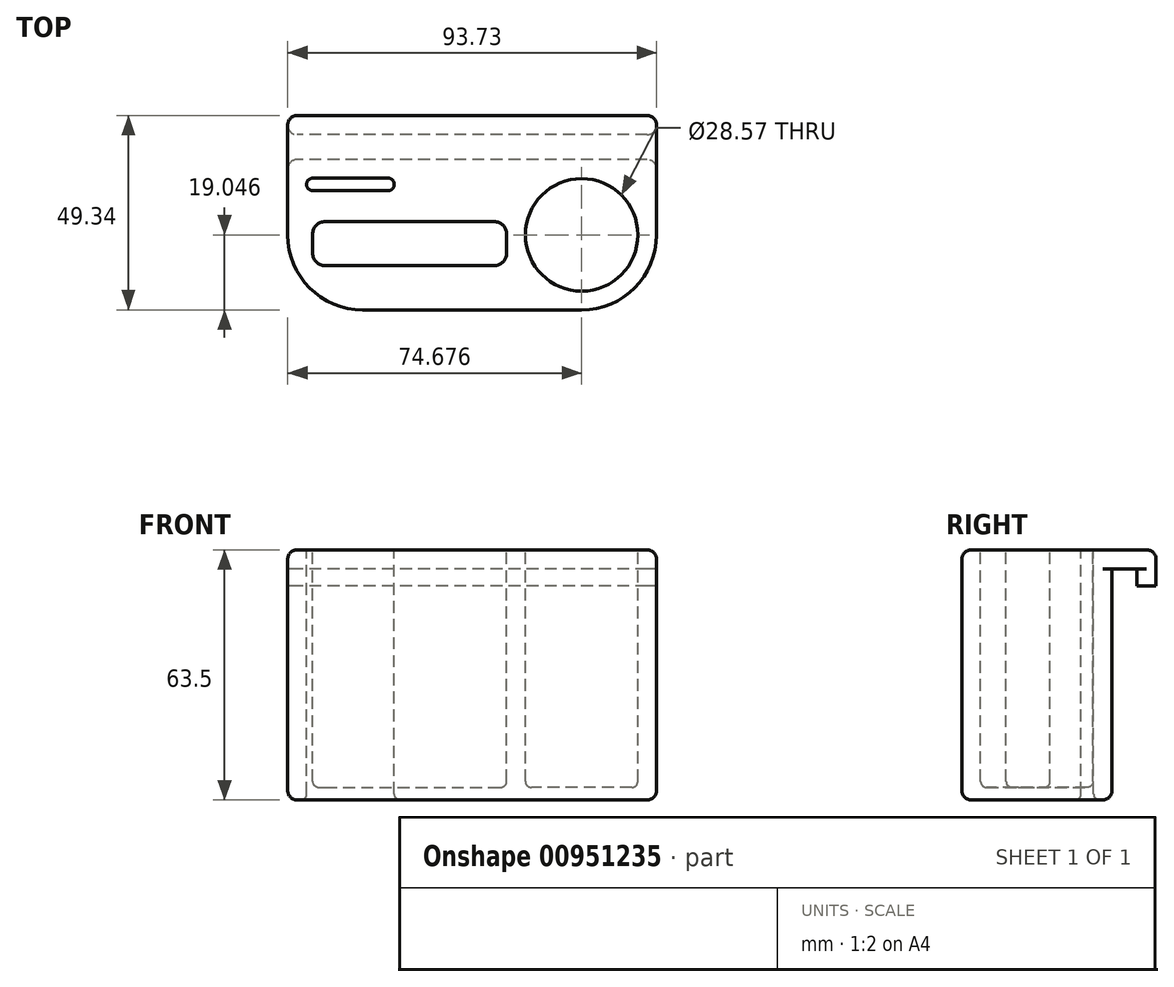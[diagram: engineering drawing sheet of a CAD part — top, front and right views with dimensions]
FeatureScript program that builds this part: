
annotation { "Feature Type Name" : "Feature", "Feature Type Description" : "" }
export const myFeature = defineFeature(function(context is Context, id is Id, definition is map)
    precondition{}
    {
        {
            var Q0;
            Q0=qCreatedBy(makeId("Right.planeOp"),FACE);
            var sketch = newSketch(context, id + "F0", { "sketchPlane" : qUnion([Q0])});
            skLineSegment(sketch, "E0", {"start": v(0, 0) * mm, "end": v(-6.35, 0) * mm});
            skLineSegment(sketch, "E1", {"start": v(-6.35, 0) * mm, "end": v(-6.35, -58.67) * mm});
            skLineSegment(sketch, "E2", {"start": v(-6.35, -58.67) * mm, "end": v(-11.18, -58.67) * mm});
            skLineSegment(sketch, "E3", {"start": v(-11.18, -58.67) * mm, "end": v(-11.18, 4.83) * mm});
            skLineSegment(sketch, "E4", {"start": v(-11.18, 4.83) * mm, "end": v(4.83, 4.83) * mm});
            skLineSegment(sketch, "E5", {"start": v(4.83, 4.83) * mm, "end": v(4.83, -4.32) * mm});
            skLineSegment(sketch, "E6", {"start": v(4.83, -4.32) * mm, "end": v(0, -4.32) * mm});
            skLineSegment(sketch, "E7", {"start": v(0, -4.32) * mm, "end": v(0, 0) * mm});
            skSolve(sketch);
        }
        {
            var Q0;
            Q0 = qSketchRegion(id + "F0", true);
            extrude(context, id + "F1", {"entities" : qUnion([Q0]), "depth" : 93.73 * mm, "offsetDistance" : 25.4 * mm});
        }
        {
            var Q0;
            Q0=makeQuery(id+"F1.opExtrude","SWEPT_FACE",FACE,{"disambiguationData":[OSD([sQuery(id+"F0.wireOp",EDGE,"E4")])]});
            var sketch = newSketch(context, id + "F2", { "sketchPlane" : qUnion([Q0])});
            skCircle(sketch, "E8", {"center": v(74.68, -25.46) * mm, "radius": 14.29 * mm});
            skLineSegment(sketch, "E9", {"start": v(93.73, -11.18) * mm, "end": v(93.73, -25.46) * mm});
            skLineSegment(sketch, "E10", {"start": v(74.68, -44.51) * mm, "end": v(19.05, -44.51) * mm});
            skLineSegment(sketch, "E11", {"start": v(0, -25.46) * mm, "end": v(0, -11.18) * mm});
            skLineSegment(sketch, "E12", {"start": v(0, -11.18) * mm, "end": v(93.73, -11.18) * mm});
            skPoint(sketch, "E13.visualSharp", {"position": v(93.73, -44.51) * mm});
            skArc(sketch, "E13.filletArc", {"start": v(74.68, -44.51) * mm, "mid": v(88.15, -38.93) * mm, "end": v(93.73, -25.46) * mm});
            skPoint(sketch, "E14.visualSharp", {"position": v(0, -44.51) * mm});
            skArc(sketch, "E14.filletArc", {"start": v(0, -25.46) * mm, "mid": v(5.58, -38.93) * mm, "end": v(19.05, -44.51) * mm});
            skSolve(sketch);
        }
        {
            var Q0;
            Q0 = qSketchRegion(id + "F2", true);
            var Q1;
            Q1=makeQuery(id+"F1.opExtrude","SWEPT_FACE",FACE,{"disambiguationData":[OSD([sQuery(id+"F0.wireOp",EDGE,"E2")])]});
            extrude(context, id + "F3", {"entities" : qUnion([Q0]), "operationType" : NewBodyOperationType.ADD, "endBound" : BoundingType.UP_TO_SURFACE, "oppositeDirection" : true, "depth" : 25.4 * mm, "endBoundEntityFace" : qUnion([Q1]), "offsetDistance" : 25.4 * mm});
        }
        {
            var Q0;
            Q0=makeQuery(id+"F2.imprint","IMPRINT",FACE,{"disambiguationData":[TD([[makeQuery(id+"F2.imprint","IMPRINT",EDGE,{"derivedFrom":sQuery(id+"F2.wireOp",EDGE,"E8")}),1.0]])]});
            var Q1;
            Q1=sQuery(id+"F2.wireOp",EDGE,"E8");
            extrude(context, id + "F4", {"entities" : qUnion([Q0]), "operationType" : NewBodyOperationType.REMOVE, "surfaceEntities" : qUnion([Q1]), "oppositeDirection" : true, "depth" : 60.32 * mm, "offsetDistance" : 25.4 * mm});
        }
        {
            var Q0;
            {var subQ2=sQuery(id+"F2.wireOp",EDGE,"E8");Q0=makeQuery(id+"F2.imprint","IMPRINT",FACE,{"disambiguationData":[TD([[makeQuery(id+"F2.imprint","IMPRINT",EDGE,{"derivedFrom":subQ2}),-1.0]])]});}
            var sketch = newSketch(context, id + "F5", { "sketchPlane" : qUnion([Q0])});
            skLineSegment(sketch, "E15.bottom", {"start": v(6.35, -11.05) * mm, "end": v(25.53, -11.05) * mm});
            skLineSegment(sketch, "E15.top", {"start": v(6.35, -14.22) * mm, "end": v(25.53, -14.22) * mm});
            skLineSegment(sketch, "E15.left", {"start": v(4.83, -12.57) * mm, "end": v(4.83, -12.7) * mm});
            skLineSegment(sketch, "E15.right", {"start": v(27.05, -12.57) * mm, "end": v(27.05, -12.7) * mm});
            skPoint(sketch, "E16.visualSharp", {"position": v(4.83, -11.05) * mm});
            skArc(sketch, "E16.filletArc", {"start": v(6.35, -11.05) * mm, "mid": v(5.27, -11.5) * mm, "end": v(4.83, -12.57) * mm});
            skPoint(sketch, "E17.visualSharp", {"position": v(4.83, -14.22) * mm});
            skArc(sketch, "E17.filletArc", {"start": v(4.83, -12.7) * mm, "mid": v(5.27, -13.78) * mm, "end": v(6.35, -14.22) * mm});
            skPoint(sketch, "E18.visualSharp", {"position": v(27.05, -14.22) * mm});
            skArc(sketch, "E18.filletArc", {"start": v(25.53, -14.22) * mm, "mid": v(26.6, -13.78) * mm, "end": v(27.05, -12.7) * mm});
            skPoint(sketch, "E19.visualSharp", {"position": v(27.05, -11.05) * mm});
            skArc(sketch, "E19.filletArc", {"start": v(27.05, -12.57) * mm, "mid": v(26.6, -11.5) * mm, "end": v(25.53, -11.05) * mm});
            skSolve(sketch);
        }
        {
            var Q0;
            Q0 = qSketchRegion(id + "F5", true);
            extrude(context, id + "F6", {"entities" : qUnion([Q0]), "operationType" : NewBodyOperationType.REMOVE, "endBound" : BoundingType.THROUGH_ALL, "oppositeDirection" : true, "depth" : 25.4 * mm, "offsetDistance" : 25.4 * mm});
        }
        {
            var Q0;
            Q0=makeQuery(id+"F3.boolean.opBoolean","MERGE",FACE,{"derivedFrom":[makeQuery(id+"F1.opExtrude","SWEPT_FACE",FACE,{"disambiguationData":[OSD([sQuery(id+"F0.wireOp",EDGE,"E4")])]}),makeQuery(id+"F3.opExtrude","CAP_FACE",FACE,{"disambiguationData":[OSD([sQuery(id+"F2.wireOp",EDGE,"E9"),sQuery(id+"F2.wireOp",EDGE,"E10"),sQuery(id+"F2.wireOp",EDGE,"E11"),sQuery(id+"F2.wireOp",EDGE,"E12"),sQuery(id+"F2.wireOp",EDGE,"E13.filletArc"),sQuery(id+"F2.wireOp",EDGE,"E14.filletArc")])],"isStart":true})]});
            var sketch = newSketch(context, id + "F7", { "sketchPlane" : qUnion([Q0])});
            skLineSegment(sketch, "E20.bottom", {"start": v(52.45, -22.1) * mm, "end": v(9.53, -22.1) * mm});
            skLineSegment(sketch, "E20.top", {"start": v(52.45, -33.27) * mm, "end": v(9.53, -33.27) * mm});
            skLineSegment(sketch, "E20.left", {"start": v(55.63, -25.27) * mm, "end": v(55.63, -30.1) * mm});
            skLineSegment(sketch, "E20.right", {"start": v(6.35, -25.27) * mm, "end": v(6.35, -30.1) * mm});
            skPoint(sketch, "E21.visualSharp", {"position": v(6.35, -22.1) * mm});
            skArc(sketch, "E21.filletArc", {"start": v(9.53, -22.1) * mm, "mid": v(7.28, -23.03) * mm, "end": v(6.35, -25.27) * mm});
            skPoint(sketch, "E22.visualSharp", {"position": v(6.35, -33.27) * mm});
            skArc(sketch, "E22.filletArc", {"start": v(6.35, -30.1) * mm, "mid": v(7.28, -32.34) * mm, "end": v(9.53, -33.27) * mm});
            skPoint(sketch, "E23.visualSharp", {"position": v(55.63, -33.27) * mm});
            skArc(sketch, "E23.filletArc", {"start": v(52.45, -33.27) * mm, "mid": v(54.7, -32.34) * mm, "end": v(55.63, -30.1) * mm});
            skPoint(sketch, "E24.visualSharp", {"position": v(55.63, -22.1) * mm});
            skArc(sketch, "E24.filletArc", {"start": v(55.63, -25.27) * mm, "mid": v(54.7, -23.03) * mm, "end": v(52.45, -22.1) * mm});
            skSolve(sketch);
        }
        {
            var Q0;
            Q0 = qSketchRegion(id + "F7", true);
            var Q1;
            Q1=makeQuery(id+"F4.boolean.opBoolean","COPY",FACE,{"derivedFrom":makeQuery(id+"F4.opExtrude","CAP_FACE",FACE,{"disambiguationData":[OSD([sQuery(id+"F2.wireOp",EDGE,"E8")])],"isStart":false})});
            extrude(context, id + "F8", {"entities" : qUnion([Q0]), "operationType" : NewBodyOperationType.REMOVE, "endBound" : BoundingType.UP_TO_SURFACE, "oppositeDirection" : true, "depth" : 25.4 * mm, "endBoundEntityFace" : qUnion([Q1]), "offsetDistance" : 25.4 * mm});
        }
        {
            var Q0;
            Q0=makeQuery(id+"F1.opExtrude","SWEPT_EDGE",EDGE,{"disambiguationData":[OSD([sQuery(id+"F0.wireOp",EDGE,"E4"),sQuery(id+"F0.wireOp",EDGE,"E5")])]});
            var Q1;
            Q1=makeQuery(id+"F3.boolean.opBoolean","MERGE",EDGE,{"derivedFrom":[makeQuery(id+"F1.opExtrude","CAP_EDGE",EDGE,{"disambiguationData":[OSD([sQuery(id+"F0.wireOp",EDGE,"E4")])],"isStart":true}),makeQuery(id+"F3.opExtrude","CAP_EDGE",EDGE,{"disambiguationData":[OSD([sQuery(id+"F2.wireOp",EDGE,"E11")])],"isStart":true})]});
            var Q2;
            Q2=makeQuery(id+"F1.opExtrude","CAP_EDGE",EDGE,{"disambiguationData":[OSD([sQuery(id+"F0.wireOp",EDGE,"E5")])],"isStart":true});
            var Q3;
            Q3=makeQuery(id+"F1.opExtrude","CAP_EDGE",EDGE,{"disambiguationData":[OSD([sQuery(id+"F0.wireOp",EDGE,"E5")])],"isStart":false});
            var Q4;
            Q4=makeQuery(id+"F4.boolean.opBoolean","COPY",EDGE,{"derivedFrom":makeQuery(id+"F4.opExtrude","CAP_EDGE",EDGE,{"disambiguationData":[OSD([sQuery(id+"F2.wireOp",EDGE,"E8")])],"isStart":true})});
            var Q5;
            Q5=makeQuery(id+"F1.opExtrude","CAP_EDGE",EDGE,{"disambiguationData":[OSD([sQuery(id+"F0.wireOp",EDGE,"E1")])],"isStart":true});
            var Q6;
            Q6=makeQuery(id+"F1.opExtrude","CAP_EDGE",EDGE,{"disambiguationData":[OSD([sQuery(id+"F0.wireOp",EDGE,"E1")])],"isStart":false});
            var Q7;
            Q7=makeQuery(id+"F1.opExtrude","SWEPT_EDGE",EDGE,{"disambiguationData":[OSD([sQuery(id+"F0.wireOp",EDGE,"E1"),sQuery(id+"F0.wireOp",EDGE,"E2")])]});
            var Q8;
            Q8=makeQuery(id+"F3.boolean.opBoolean","MERGE",EDGE,{"derivedFrom":[makeQuery(id+"F1.opExtrude","CAP_EDGE",EDGE,{"disambiguationData":[OSD([sQuery(id+"F0.wireOp",EDGE,"E2")])],"isStart":true}),makeQuery(id+"F3.opExtrude","CAP_EDGE",EDGE,{"disambiguationData":[OSD([sQuery(id+"F2.wireOp",EDGE,"E11")])],"isStart":false})]});
            var Q9;
            Q9=makeQuery(id+"F1.opExtrude","CAP_EDGE",EDGE,{"disambiguationData":[OSD([sQuery(id+"F0.wireOp",EDGE,"E7")])],"isStart":true});
            var Q10;
            Q10=makeQuery(id+"F1.opExtrude","CAP_EDGE",EDGE,{"disambiguationData":[OSD([sQuery(id+"F0.wireOp",EDGE,"E7")])],"isStart":false});
            fillet(context, id + "F9", {"entities" : qUnion([Q0, Q1, Q2, Q3, Q4, Q5, Q6, Q7, Q8, Q9, Q10]), "radius" : 2.4 * mm, "tangentPropagation" : true, "allowEdgeOverflow" : false});
        }
        {
            var Q0;
            Q0=makeQuery(id+"F6.boolean.opBoolean","COPY",EDGE,{"derivedFrom":makeQuery(id+"F6.opExtrude","CAP_EDGE",EDGE,{"disambiguationData":[OSD([sQuery(id+"F5.wireOp",EDGE,"E15.bottom")])],"isStart":true})});
            var Q1;
            Q1=makeQuery(id+"F6.boolean.opBoolean","INTERSECT",EDGE,{"derivedFrom":[makeQuery(id+"F3.boolean.opBoolean","MERGE",FACE,{"derivedFrom":[makeQuery(id+"F1.opExtrude","SWEPT_FACE",FACE,{"disambiguationData":[OSD([sQuery(id+"F0.wireOp",EDGE,"E2")])]}),makeQuery(id+"F3.opExtrude","CAP_FACE",FACE,{"disambiguationData":[OSD([sQuery(id+"F2.wireOp",EDGE,"E9"),sQuery(id+"F2.wireOp",EDGE,"E10"),sQuery(id+"F2.wireOp",EDGE,"E11"),sQuery(id+"F2.wireOp",EDGE,"E12"),sQuery(id+"F2.wireOp",EDGE,"E13.filletArc"),sQuery(id+"F2.wireOp",EDGE,"E14.filletArc")])],"isStart":false})]}),makeQuery(id+"F6.opExtrude","SWEPT_FACE",FACE,{"disambiguationData":[OSD([sQuery(id+"F5.wireOp",EDGE,"E18.filletArc")])]})]});
            var Q2;
            Q2=makeQuery(id+"F8.boolean.opBoolean","COPY",EDGE,{"derivedFrom":makeQuery(id+"F8.opExtrude","CAP_EDGE",EDGE,{"disambiguationData":[OSD([sQuery(id+"F7.wireOp",EDGE,"E20.bottom")])],"isStart":true})});
            var Q3;
            Q3=makeQuery(id+"F8.boolean.opBoolean","COPY",EDGE,{"derivedFrom":makeQuery(id+"F8.opExtrude","CAP_EDGE",EDGE,{"disambiguationData":[OSD([sQuery(id+"F7.wireOp",EDGE,"E20.top")])],"isStart":false})});
            var Q4;
            Q4=makeQuery(id+"F4.boolean.opBoolean","COPY",EDGE,{"derivedFrom":makeQuery(id+"F4.opExtrude","CAP_EDGE",EDGE,{"disambiguationData":[OSD([sQuery(id+"F2.wireOp",EDGE,"E8")])],"isStart":false})});
            fillet(context, id + "F10", {"entities" : qUnion([Q0, Q1, Q2, Q3, Q4]), "radius" : 1.52 * mm, "tangentPropagation" : true, "allowEdgeOverflow" : false});
        }
    });
